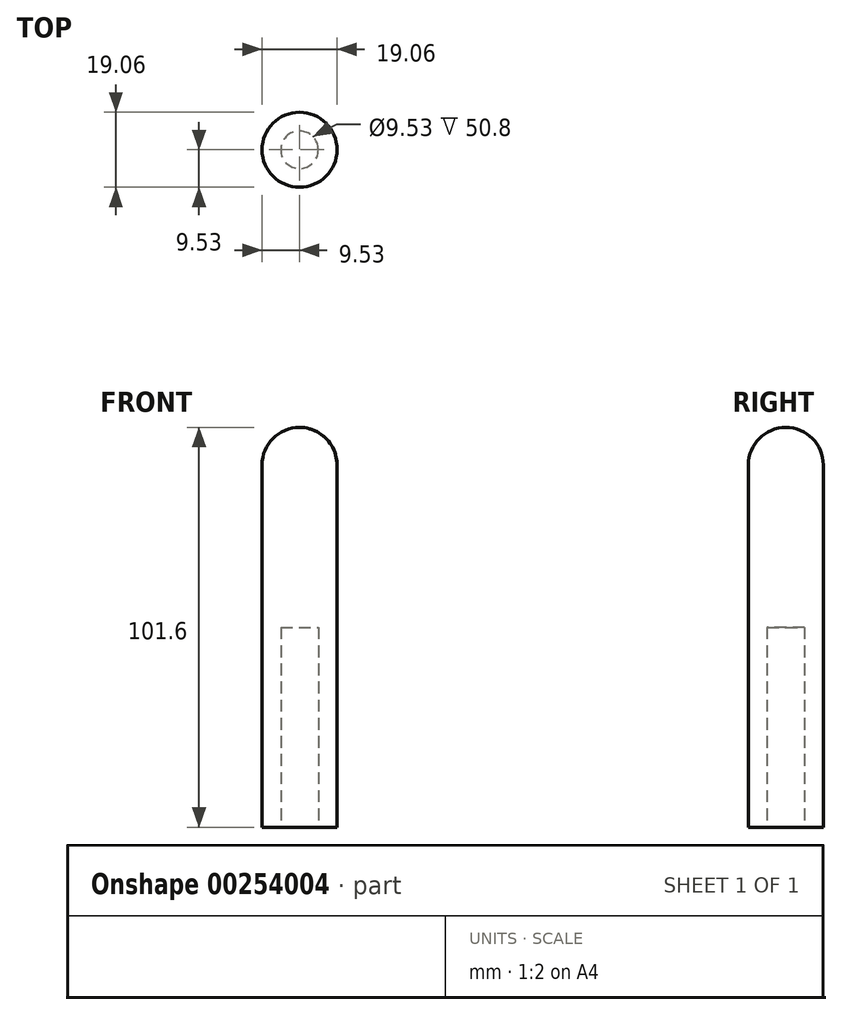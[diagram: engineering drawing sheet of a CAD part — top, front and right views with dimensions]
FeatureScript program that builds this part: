
annotation { "Feature Type Name" : "Feature", "Feature Type Description" : "" }
export const myFeature = defineFeature(function(context is Context, id is Id, definition is map)
    precondition{}
    {
        {
            var Q0;
            Q0=qCreatedBy(makeId("Top.planeOp"),FACE);
            var sketch = newSketch(context, id + "F0", { "sketchPlane" : qUnion([Q0])});
            skCircle(sketch, "E0", {"center": v(0, 0) * mm, "radius": 9.53 * mm});
            skSolve(sketch);
        }
        {
            var Q0;
            Q0 = qSketchRegion(id + "F0", true);
            extrude(context, id + "F1", {"entities" : qUnion([Q0]), "depth" : 101.6 * mm});
        }
        {
            var Q0;
            Q0=makeQuery(id+"F1.opExtrude","CAP_FACE",FACE,{"disambiguationData":[OSD([sQuery(id+"F0.wireOp",EDGE,"E0")])],"isStart":true});
            var sketch = newSketch(context, id + "F2", { "sketchPlane" : qUnion([Q0])});
            skCircle(sketch, "E1", {"center": v(0, 0) * mm, "radius": 4.76 * mm});
            skSolve(sketch);
        }
        {
            var Q0;
            Q0 = qSketchRegion(id + "F2", true);
            extrude(context, id + "F3", {"entities" : qUnion([Q0]), "operationType" : NewBodyOperationType.REMOVE, "oppositeDirection" : true, "depth" : 50.8 * mm});
        }
        {
            var Q0;
            Q0=makeQuery(id+"F1.opExtrude","CAP_EDGE",EDGE,{"disambiguationData":[OSD([sQuery(id+"F0.wireOp",EDGE,"E0")])],"isStart":false});
            fillet(context, id + "F4", {"entities" : qUnion([Q0]), "radius" : 9.52 * mm, "tangentPropagation" : true, "allowEdgeOverflow" : false});
        }
    });
